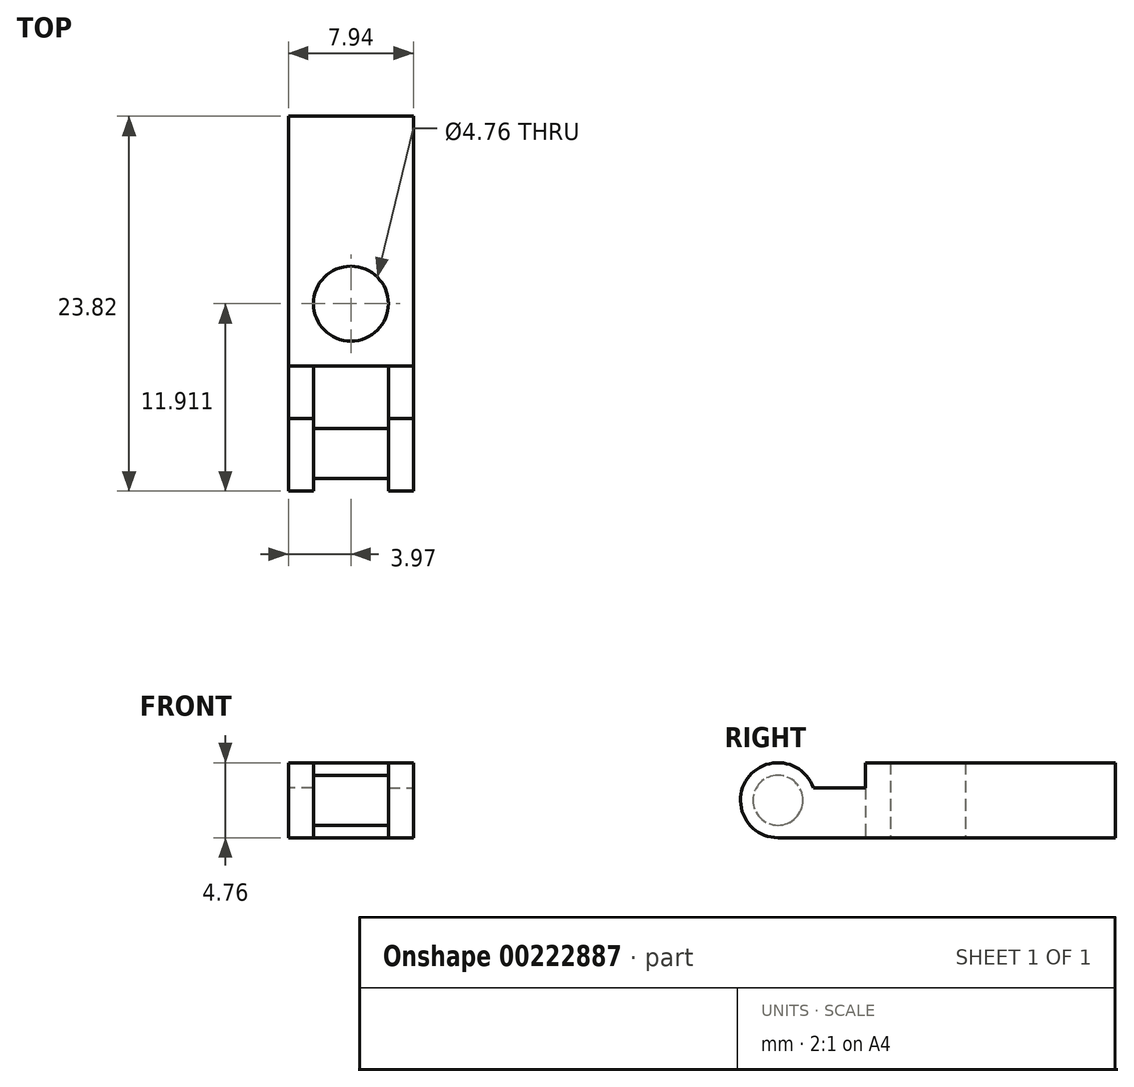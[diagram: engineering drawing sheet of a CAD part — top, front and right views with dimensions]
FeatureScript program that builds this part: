
annotation { "Feature Type Name" : "Feature", "Feature Type Description" : "" }
export const myFeature = defineFeature(function(context is Context, id is Id, definition is map)
    precondition{}
    {
        {
            var Q0;
            Q0=qCreatedBy(makeId("Top.planeOp"),FACE);
            var sketch = newSketch(context, id + "F0", { "sketchPlane" : qUnion([Q0])});
            skLineSegment(sketch, "E0.bottom", {"start": v(-3.97, 7.94) * mm, "end": v(3.97, 7.94) * mm});
            skLineSegment(sketch, "E0.top", {"start": v(-3.97, -7.94) * mm, "end": v(3.97, -7.94) * mm});
            skLineSegment(sketch, "E0.left", {"start": v(-3.97, 7.94) * mm, "end": v(-3.97, -7.94) * mm});
            skLineSegment(sketch, "E0.right", {"start": v(3.97, 7.94) * mm, "end": v(3.97, -7.94) * mm});
            skPoint(sketch, "E0.middle", {"position": v(0, 0) * mm});
            skCircle(sketch, "E1", {"center": v(0, 3.97) * mm, "radius": 2.38 * mm});
            skCircle(sketch, "E2.MirrorC", {"center": v(0, -3.97) * mm, "radius": 2.38 * mm});
            skSolve(sketch);
        }
        {
            var Q0;
            Q0 = qSketchRegion(id + "F0", true);
            extrude(context, id + "F1", {"entities" : qUnion([Q0]), "depth" : 3.17 * mm});
        }
        {
            var Q0;
            Q0=makeQuery(id+"F0.imprint","IMPRINT",FACE,{"disambiguationData":[TD([[makeQuery(id+"F0.imprint","IMPRINT",EDGE,{"derivedFrom":sQuery(id+"F0.wireOp",EDGE,"E1")}),1.0]])]});
            var Q1;
            Q1=makeQuery(id+"F0.imprint","IMPRINT",FACE,{"disambiguationData":[TD([[makeQuery(id+"F0.imprint","IMPRINT",EDGE,{"derivedFrom":sQuery(id+"F0.wireOp",EDGE,"E2.MirrorC")}),-1.0]])]});
            extrude(context, id + "F2", {"entities" : qUnion([Q0, Q1]), "operationType" : NewBodyOperationType.ADD, "depth" : 4.76 * mm});
        }
        {
            var Q0;
            Q0=makeQuery(id+"F1.opExtrude","SWEPT_FACE",FACE,{"disambiguationData":[OSD([sQuery(id+"F0.wireOp",EDGE,"E0.left")])]});
            var sketch = newSketch(context, id + "F3", { "sketchPlane" : qUnion([Q0])});
            skLineSegment(sketch, "E3.bottom", {"start": v(7.94, 0) * mm, "end": v(11.11, 0) * mm});
            skLineSegment(sketch, "E3.top", {"start": v(7.94, 3.18) * mm, "end": v(11.11, 3.18) * mm});
            skLineSegment(sketch, "E3.left", {"start": v(7.94, 0) * mm, "end": v(7.94, 3.18) * mm});
            skLineSegment(sketch, "E3.right", {"start": v(11.11, 0) * mm, "end": v(11.11, 3.18) * mm});
            skLineSegment(sketch, "E4", {"start": v(13.5, 0) * mm, "end": v(13.5, 2.38) * mm});
            skCircle(sketch, "E5", {"center": v(13.5, 2.38) * mm, "radius": 2.38 * mm});
            skLineSegment(sketch, "E6", {"start": v(11.11, 3.18) * mm, "end": v(11.25, 3.18) * mm});
            skLineSegment(sketch, "E7", {"start": v(11.11, 0) * mm, "end": v(13.5, 0) * mm});
            skSolve(sketch);
        }
        {
            var Q0;
            Q0 = qSketchRegion(id + "F3", true);
            extrude(context, id + "F4", {"entities" : qUnion([Q0]), "operationType" : NewBodyOperationType.ADD, "oppositeDirection" : true, "depth" : 1.59 * mm});
        }
        {
            var Q0;
            Q0=makeQuery(id+"F1.opExtrude","SWEPT_BODY",BODY,{"disambiguationData":[OSD([sQuery(id+"F0.wireOp",EDGE,"E0.bottom"),sQuery(id+"F0.wireOp",EDGE,"E0.top"),sQuery(id+"F0.wireOp",EDGE,"E0.left"),sQuery(id+"F0.wireOp",EDGE,"E0.right"),sQuery(id+"F0.wireOp",EDGE,"E1"),sQuery(id+"F0.wireOp",EDGE,"E2.MirrorC")])]});
            var Q1;
            Q1=qCreatedBy(makeId("Right.planeOp"),FACE);
            mirror(context, id + "F5", {"operationType" : NewBodyOperationType.ADD, "entities" : qUnion([Q0]), "mirrorPlane" : qUnion([Q1])});
        }
        {
            var Q0;
            Q0=makeQuery(id+"F4.opExtrude","CAP_FACE",FACE,{"disambiguationData":[OSD([sQuery(id+"F3.wireOp",EDGE,"E3.bottom"),sQuery(id+"F3.wireOp",EDGE,"E3.top"),sQuery(id+"F3.wireOp",EDGE,"E3.left"),sQuery(id+"F3.wireOp",EDGE,"E5"),sQuery(id+"F3.wireOp",EDGE,"E6"),sQuery(id+"F3.wireOp",EDGE,"E7")])],"isStart":false});
            var sketch = newSketch(context, id + "F6", { "sketchPlane" : qUnion([Q0])});
            skCircle(sketch, "E8", {"center": v(-13.5, 2.38) * mm, "radius": 1.59 * mm});
            skSolve(sketch);
        }
        {
            var Q0;
            Q0 = qSketchRegion(id + "F6", true);
            extrude(context, id + "F7", {"entities" : qUnion([Q0]), "operationType" : NewBodyOperationType.ADD, "depth" : 4.76 * mm});
        }
    });
